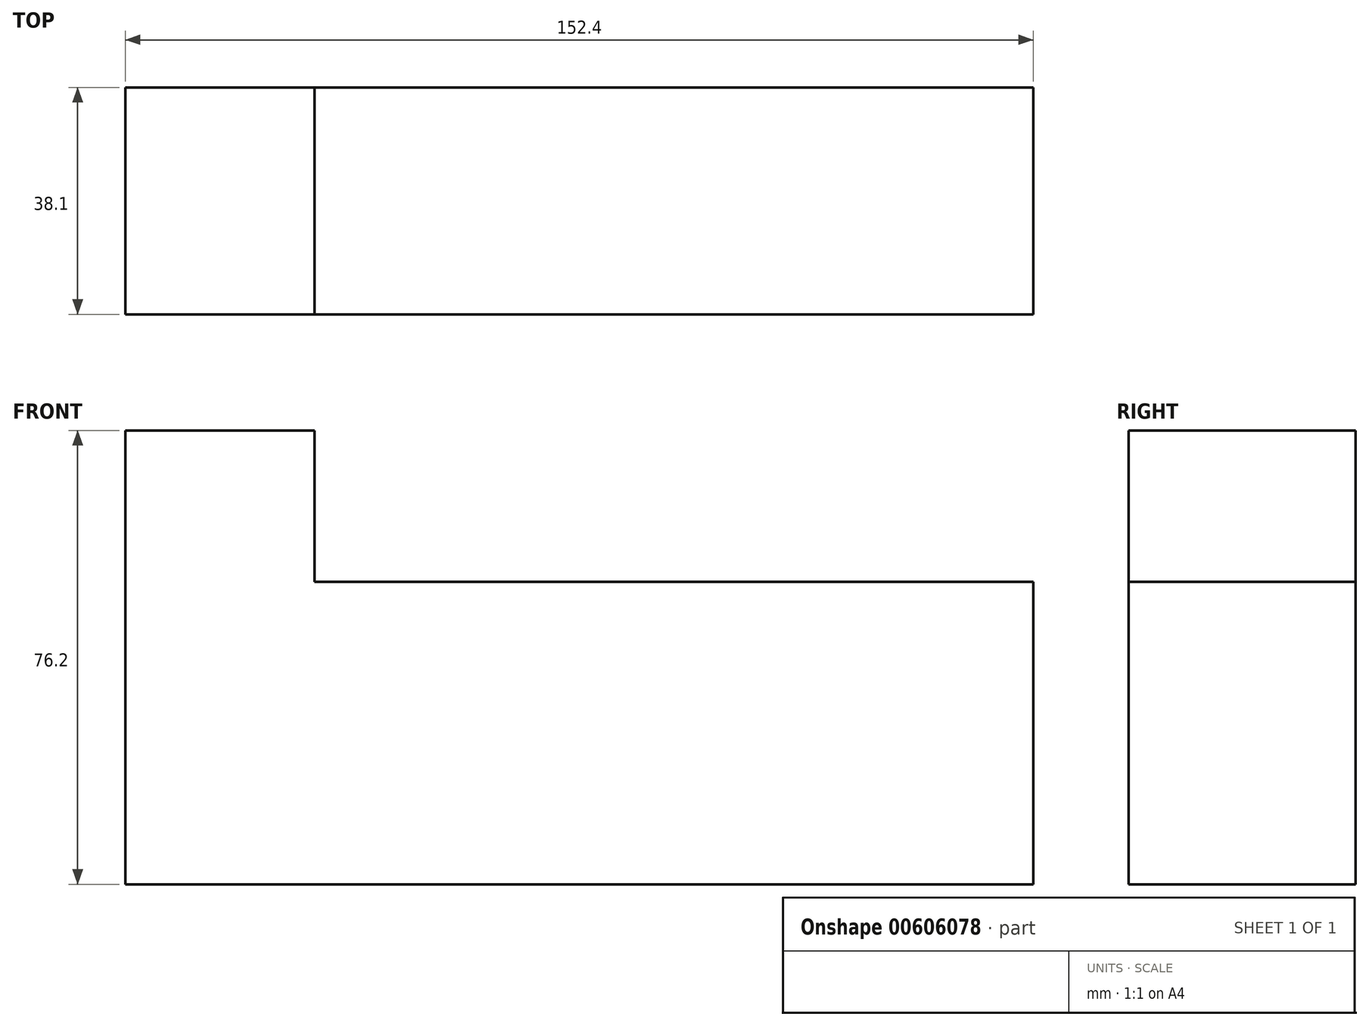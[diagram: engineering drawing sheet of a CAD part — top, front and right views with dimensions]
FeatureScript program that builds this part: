
annotation { "Feature Type Name" : "Feature", "Feature Type Description" : "" }
export const myFeature = defineFeature(function(context is Context, id is Id, definition is map)
    precondition{}
    {
        {
            var Q0;
            Q0=qCreatedBy(makeId("Front.planeOp"),FACE);
            var sketch = newSketch(context, id + "F0", { "sketchPlane" : qUnion([Q0])});
            skLineSegment(sketch, "E0", {"start": v(-44.13, -18.27) * mm, "end": v(108.27, -18.27) * mm});
            skLineSegment(sketch, "E1", {"start": v(108.27, -18.27) * mm, "end": v(108.27, 32.53) * mm});
            skLineSegment(sketch, "E2", {"start": v(108.27, 32.53) * mm, "end": v(-12.38, 32.53) * mm});
            skLineSegment(sketch, "E3", {"start": v(-12.38, 32.53) * mm, "end": v(-12.38, 57.93) * mm});
            skLineSegment(sketch, "E4", {"start": v(-44.13, -18.27) * mm, "end": v(-44.13, 57.93) * mm});
            skLineSegment(sketch, "E5", {"start": v(-44.13, 57.93) * mm, "end": v(-12.38, 57.93) * mm});
            skSolve(sketch);
        }
        {
            var Q0;
            Q0=makeQuery(id+"F0.imprint","IMPRINT",FACE,{"disambiguationData":[TD([[makeQuery(id+"F0.imprint","IMPRINT",EDGE,{"derivedFrom":sQuery(id+"F0.wireOp",EDGE,"E0")}),1.0]])]});
            extrude(context, id + "F1", {"entities" : qUnion([Q0]), "depth" : 38.1 * mm, "offsetDistance" : 25.4 * mm});
        }
    });
